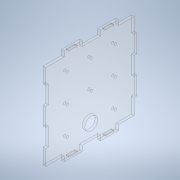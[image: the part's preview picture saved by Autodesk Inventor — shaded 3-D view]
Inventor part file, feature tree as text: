
AUTODESK INVENTOR PART (.ipt)
format: ipt  version: 2021 (Build 250183000, 183)  size: 196,608 bytes
history: native  units: mm
features: sketch x10, hole x9, extrude x1
ambient origin geometry x8: Origin, YZ Plane, XZ Plane, XY Plane, X Axis, Y Axis, Z Axis, Center Point
bodies: Solid1 (feature_tree)
feature tree (20):
  extrude  "Extrusion1"  Depth=3.0mm
  hole  "Hole2"  [1 undecoded]
  hole  "Hole3"  [1 undecoded]
  hole  "Hole4"  [1 undecoded]
  hole  "Hole5"  [1 undecoded]
  hole  "Hole6"  [1 undecoded]
  hole  "Hole7"  [1 undecoded]
  hole  "Hole8"  [1 undecoded]
  hole  "Hole9"  [1 undecoded]
  hole  "Hole10"  [1 undecoded]
  sketch  "Sketch1"  dims[d4=3.0mm d5=0.0mm d22=3.0mm]
  sketch  "Sketch3"  dims[d23=3.0mm d24=6.0mm d25=4.0mm d26=2.0mm d27=90.0deg d28=8.0mm d29=20.594885mm d30=3.0mm]
  sketch  "Sketch4"  dims[d31=3.0mm d32=6.0mm d33=4.0mm d34=2.0mm d35=90.0deg d36=8.0mm d37=20.594885mm d38=3.0mm]
  sketch  "Sketch5"  dims[d39=3.0mm d40=6.0mm d41=4.0mm d42=2.0mm d43=90.0deg d44=8.0mm d45=20.594885mm d46=3.0mm]
  sketch  "Sketch6"  dims[d47=15.0mm d48=6.0mm d49=4.0mm d50=2.0mm d51=90.0deg d52=8.0mm d53=20.594885mm d54=3.0mm]
  sketch  "Sketch7"  dims[d55=3.0mm d56=6.0mm d57=4.0mm d58=2.0mm d59=90.0deg d60=8.0mm d61=20.594885mm d62=3.0mm]
  sketch  "Sketch8"  dims[d63=3.0mm d64=6.0mm d65=4.0mm d66=2.0mm d67=90.0deg d68=8.0mm d69=20.594885mm d70=3.0mm]
  sketch  "Sketch9"  dims[d71=3.0mm d72=6.0mm d73=4.0mm d74=2.0mm d75=90.0deg d76=8.0mm d77=20.594885mm d78=3.0mm]
  sketch  "Sketch10"  dims[d79=3.0mm d80=6.0mm d81=4.0mm d82=2.0mm d83=90.0deg d84=8.0mm d85=20.594885mm d86=3.0mm]
  sketch  "Sketch11"  dims[d87=3.0mm d88=6.0mm d89=4.0mm d90=2.0mm d91=90.0deg d92=8.0mm d93=20.594885mm d94=1.0mm d95=10.0mm d96=1.0mm d97=1.0mm d98=10.0mm d99=10.0mm]
note: 9 required parameter values undecoded (feature->parameter linkage not recoverable at this tier; creation-order binding heuristic only, values carry confidence <= 0.55)
